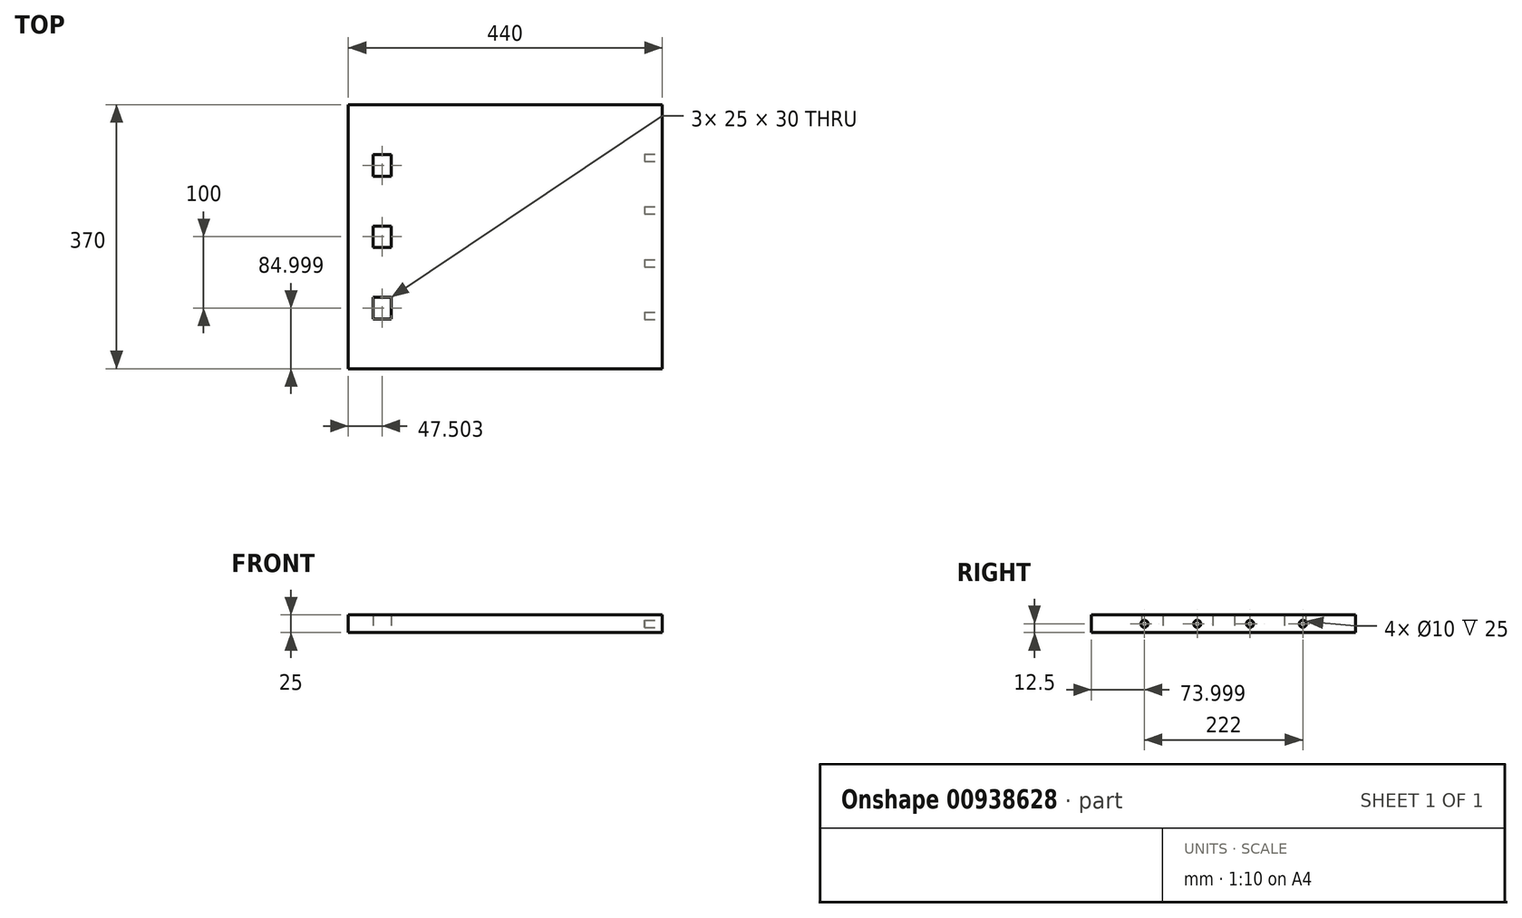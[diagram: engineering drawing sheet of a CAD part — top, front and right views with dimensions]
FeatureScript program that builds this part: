
annotation { "Feature Type Name" : "Feature", "Feature Type Description" : "" }
export const myFeature = defineFeature(function(context is Context, id is Id, definition is map)
    precondition{}
    {
        {
            var Q0;
            Q0=qCreatedBy(makeId("Top.planeOp"),FACE);
            var sketch = newSketch(context, id + "F0", { "sketchPlane" : qUnion([Q0])});
            skLineSegment(sketch, "E0.bottom", {"start": v(-325.96, -188.72) * mm, "end": v(114.04, -188.72) * mm});
            skLineSegment(sketch, "E0.top", {"start": v(-325.96, 181.28) * mm, "end": v(114.04, 181.28) * mm});
            skLineSegment(sketch, "E0.left", {"start": v(-325.96, -188.72) * mm, "end": v(-325.96, 181.28) * mm});
            skLineSegment(sketch, "E0.right", {"start": v(114.04, -188.72) * mm, "end": v(114.04, 181.28) * mm});
            skLineSegment(sketch, "E1.bottom", {"start": v(-290.96, 111.28) * mm, "end": v(-265.96, 111.28) * mm});
            skLineSegment(sketch, "E1.top", {"start": v(-290.96, 81.28) * mm, "end": v(-265.96, 81.28) * mm});
            skLineSegment(sketch, "E1.left", {"start": v(-290.96, 111.28) * mm, "end": v(-290.96, 81.28) * mm});
            skLineSegment(sketch, "E1.right", {"start": v(-265.96, 111.28) * mm, "end": v(-265.96, 81.28) * mm});
            skLineSegment(sketch, "E2.bottom", {"start": v(-290.96, -118.72) * mm, "end": v(-265.96, -118.72) * mm});
            skLineSegment(sketch, "E2.top", {"start": v(-290.96, -88.72) * mm, "end": v(-265.96, -88.72) * mm});
            skLineSegment(sketch, "E2.left", {"start": v(-290.96, -118.72) * mm, "end": v(-290.96, -88.72) * mm});
            skLineSegment(sketch, "E2.right", {"start": v(-265.96, -118.72) * mm, "end": v(-265.96, -88.72) * mm});
            skLineSegment(sketch, "E3.bottom", {"start": v(-290.96, 11.28) * mm, "end": v(-265.96, 11.28) * mm});
            skLineSegment(sketch, "E3.top", {"start": v(-290.96, -18.72) * mm, "end": v(-265.96, -18.72) * mm});
            skLineSegment(sketch, "E3.left", {"start": v(-290.96, 11.28) * mm, "end": v(-290.96, -18.72) * mm});
            skLineSegment(sketch, "E3.right", {"start": v(-265.96, 11.28) * mm, "end": v(-265.96, -18.72) * mm});
            skSolve(sketch);
        }
        {
            var Q0;
            Q0=makeQuery(id+"F0.imprint","IMPRINT",FACE,{"disambiguationData":[TD([[makeQuery(id+"F0.imprint","IMPRINT",EDGE,{"derivedFrom":sQuery(id+"F0.wireOp",EDGE,"E0.bottom")}),1.0]])]});
            extrude(context, id + "F1", {"entities" : qUnion([Q0]), "depth" : 25 * mm, "offsetDistance" : 25 * mm});
        }
        {
            var Q0;
            Q0=makeQuery(id+"F1.opExtrude","SWEPT_FACE",FACE,{"disambiguationData":[OSD([sQuery(id+"F0.wireOp",EDGE,"E0.right")])]});
            var sketch = newSketch(context, id + "F2", { "sketchPlane" : qUnion([Q0])});
            skCircle(sketch, "E4", {"center": v(-114.72, 12.5) * mm, "radius": 5 * mm});
            skCircle(sketch, "E5", {"center": v(-40.72, 12.5) * mm, "radius": 5 * mm});
            skCircle(sketch, "E6", {"center": v(33.28, 12.5) * mm, "radius": 5 * mm});
            skCircle(sketch, "E7", {"center": v(107.28, 12.5) * mm, "radius": 5 * mm});
            skSolve(sketch);
        }
        {
            var Q0;
            Q0=makeQuery(id+"F2.imprint","IMPRINT",FACE,{"disambiguationData":[TD([[makeQuery(id+"F2.imprint","IMPRINT",EDGE,{"derivedFrom":sQuery(id+"F2.wireOp",EDGE,"E4")}),1.0]])]});
            var Q1;
            Q1=makeQuery(id+"F2.imprint","IMPRINT",FACE,{"disambiguationData":[TD([[makeQuery(id+"F2.imprint","IMPRINT",EDGE,{"derivedFrom":sQuery(id+"F2.wireOp",EDGE,"E5")}),1.0]])]});
            var Q2;
            Q2=makeQuery(id+"F2.imprint","IMPRINT",FACE,{"disambiguationData":[TD([[makeQuery(id+"F2.imprint","IMPRINT",EDGE,{"derivedFrom":sQuery(id+"F2.wireOp",EDGE,"E6")}),1.0]])]});
            var Q3;
            Q3=makeQuery(id+"F2.imprint","IMPRINT",FACE,{"disambiguationData":[TD([[makeQuery(id+"F2.imprint","IMPRINT",EDGE,{"derivedFrom":sQuery(id+"F2.wireOp",EDGE,"E7")}),1.0]])]});
            extrude(context, id + "F3", {"entities" : qUnion([Q0, Q1, Q2, Q3]), "operationType" : NewBodyOperationType.REMOVE, "oppositeDirection" : true, "depth" : 25 * mm, "offsetDistance" : 25 * mm});
        }
    });
